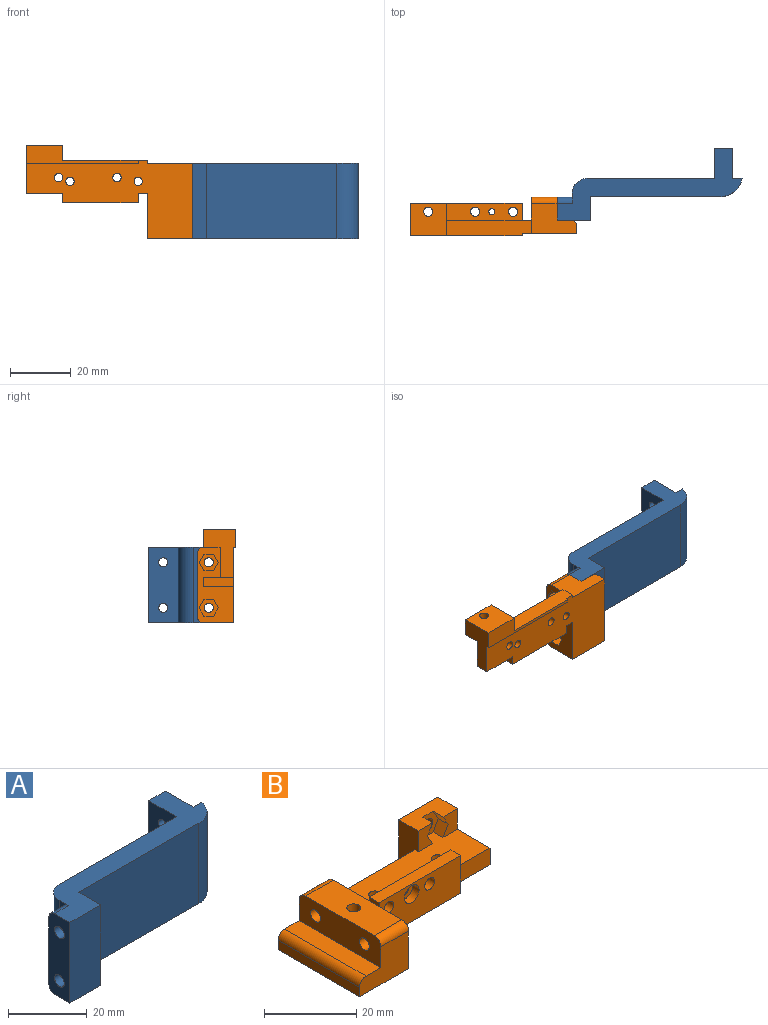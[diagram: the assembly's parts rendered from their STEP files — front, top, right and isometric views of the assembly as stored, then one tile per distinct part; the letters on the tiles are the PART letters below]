
ASSEMBLY  parts=2 mates=1
PART A: 25 faces, bbox 61x23.8x25 mm
  f0: cylinder r=1.75mm len=8mm, axis (1,0,0), area 88mm2, adj f18,f22
  f1: cylinder r=1.75mm len=8mm, axis (1,0,0), area 88mm2, adj f18,f20
  f2: plane 25x10mm, normal (-1,0,0), area 235.9mm2, adj f3,f10,f11,f12,f15,f16
  f3: plane 42x25mm, normal (0,1,0), area 1050mm2, adj f2,f11,f12,f14
  f4: plane 25x3.25mm, normal (-1,0,0), area 33mm2, adj f11,f12,f14,f17,f23,f24
  f5: plane 25x11mm, normal (0,-1,0), area 275mm2, adj f6,f11,f12,f18
  f6: plane 25x7.75mm, normal (1,0,0), area 137.2mm2, adj f5,f7,f11,f12,f19,f21
  f7: plane 43.07x25mm, normal (0,-1,0), area 1076.8mm2, adj f6,f11,f12,f13
  f8: plane 25x3mm, normal (0,1,0), area 75mm2, adj f9,f11,f12,f13
  f9: plane 25x10mm, normal (1,0,0), area 235.9mm2, adj f8,f10,f11,f12,f15,f16
  f10: plane 25x6mm, normal (0,1,0), area 150mm2, adj f2,f9,f11,f12
  f11: plane 61x23.75mm, normal (0,0,1), area 454.6mm2, adj f2,f3,f4,f5,f6,f7,f8,f9
  f12: plane 61x23.75mm, normal (0,0,-1), area 454.6mm2, adj f2,f3,f4,f5,f6,f7,f8,f9
  f13: cylinder r=7mm len=25mm, axis (0,0,1), area 249.8mm2, adj f7,f8,f11,f12
  f14: cylinder r=5mm len=25mm, axis (0,0,1), area 196.3mm2, adj f3,f4,f11,f12
  f15: cylinder r=1.5mm len=6mm, axis (1,0,0), area 56.5mm2, adj f2,f9
  f16: cylinder r=1.5mm len=6mm, axis (1,0,0), area 56.5mm2, adj f2,f9
  f17: plane 21x5mm, normal (0,1,0), area 105mm2, adj f4,f18,f23,f24
  f18: plane 25x7.5mm, normal (-1,0,0), area 166.5mm2, adj f0,f1,f5,f11,f12,f17,f23,f24
  f19: cylinder r=3mm len=6mm, axis (1,0,0), area 56.5mm2, adj f6,f20
  f20: plane 6x6mm, normal (1,0,0), area 18.7mm2, adj f1,f19
  f21: cylinder r=3mm len=6mm, axis (1,0,0), area 56.5mm2, adj f6,f22
  f22: plane 6x6mm, normal (1,0,0), area 18.7mm2, adj f0,f21
  f23: cylinder r=2mm len=5mm, axis (-1,0,0), area 15.7mm2, adj f4,f12,f17,f18
  f24: cylinder r=2mm len=5mm, axis (1,0,0), area 15.7mm2, adj f4,f11,f17,f18
PART B: 63 faces, bbox 55x31x12.8 mm
  f0: plane 5.5x4.41mm, normal (0,-1,0), area 19.9mm2, adj f1,f2,f16,f60,f61
  f1: plane 12x6mm, normal (0,0,1), area 62.5mm2, adj f0,f16,f17,f18,f42,f59,f60,f62
  f2: plane 40x13mm, normal (0,0,1), area 413.8mm2, adj f0,f5,f6,f10,f11,f15,f16,f18
  f3: cylinder r=1mm len=2mm, axis (0,-1,0), area 6.3mm2, adj f20,f34
  f4: plane 25x4.5mm, normal (0,0,1), area 112.5mm2, adj f7,f9,f22,f41
  f5: plane 28x5.25mm, normal (0,1,0), area 144.8mm2, adj f2,f6,f18,f19,f25,f26
  f6: plane 4.5x1mm, normal (-1,0,0), area 4.5mm2, adj f2,f5,f7,f19
  f7: plane 15x10mm, normal (0,1,0), area 113.4mm2, adj f4,f6,f8,f10,f19,f22,f40,f41
  f8: plane 25x2.5mm, normal (-1,0,0), area 62.5mm2, adj f7,f9,f19,f41
  f9: plane 15x10mm, normal (0,-1,0), area 113.4mm2, adj f4,f8,f10,f19,f22,f39,f41
  f10: plane 25x12mm, normal (1,0,0), area 200.9mm2, adj f2,f7,f9,f11,f19,f23,f39,f40
  f11: plane 4.5x3mm, normal (0,-1,0), area 13.5mm2, adj f2,f10,f12,f19
  f12: plane 10x3mm, normal (-1,0,0), area 30mm2, adj f11,f13,f19,f20,f21
  f13: plane 25x10mm, normal (0,-1,0), area 220mm2, adj f12,f14,f19,f21,f31,f32,f33
  f14: plane 10x3mm, normal (1,0,0), area 30mm2, adj f13,f15,f19,f20,f21
  f15: plane 12x4.5mm, normal (0,-1,0), area 54mm2, adj f2,f14,f16,f19
  f16: plane 16x10.75mm, normal (1,0,0), area 109.5mm2, adj f0,f1,f2,f15,f17,f19,f24,f26
  f17: plane 12x10.75mm, normal (0,1,0), area 121.9mm2, adj f1,f16,f18,f26,f43
  f18: plane 10.75x6mm, normal (-1,0,0), area 59.2mm2, adj f1,f2,f5,f17,f26,f42
  f19: plane 55x26mm, normal (0,0,-1), area 829.2mm2, adj f5,f6,f7,f8,f9,f10,f11,f12
  f20: plane 25x5.5mm, normal (0,1,0), area 120.2mm2, adj f2,f3,f12,f14,f21,f31,f32
  f21: plane 25x3mm, normal (0,0,1), area 75mm2, adj f12,f13,f14,f20
  f22: plane 25x7.5mm, normal (-1,0,0), area 171.6mm2, adj f4,f7,f9,f23,f35,f36,f39,f40
  f23: plane 21x8.5mm, normal (0,0,1), area 171.4mm2, adj f10,f22,f37,f39,f40
  f24: plane 37x0.75mm, normal (0,-1,0), area 27.7mm2, adj f16,f19,f25,f26
  f25: plane 1x0.75mm, normal (-1,0,0), area 0.8mm2, adj f5,f19,f24,f26
  f26: plane 37x6mm, normal (0,0,-1), area 97mm2, adj f5,f16,f17,f18,f24,f25
  f27: cylinder r=1.38mm len=4.5mm, axis (0,0,1), area 38.9mm2, adj f2,f19
  f28: cylinder r=1.38mm len=4.5mm, axis (0,0,1), area 38.9mm2, adj f2,f19
  f29: cylinder r=1.38mm len=4.5mm, axis (0,0,1), area 38.9mm2, adj f2,f19
  f30: cylinder r=1.38mm len=4.5mm, axis (0,0,1), area 38.9mm2, adj f2,f19
  f31: cylinder r=1.5mm len=3mm, axis (0,-1,0), area 28.3mm2, adj f13,f20
  f32: cylinder r=1.5mm len=3mm, axis (0,-1,0), area 28.3mm2, adj f13,f20
  f33: cylinder r=2.25mm len=4.5mm, axis (0,-1,0), area 28.3mm2, adj f13,f34
  f34: plane 4.5x4.5mm, normal (0,-1,0), area 12.8mm2, adj f3,f33
  f35: cylinder r=1.5mm len=4mm, axis (-1,0,0), area 37.7mm2, adj f22,f51
  f36: cylinder r=1.5mm len=4mm, axis (-1,0,0), area 37.7mm2, adj f22,f44
  f37: cylinder r=1.5mm len=7.5mm, axis (0,0,1), area 70.7mm2, adj f23,f38
  f38: plane 3x3mm, normal (0,0,1), area 7.1mm2, adj f37
  f39: cylinder r=2mm len=8.5mm, axis (-1,0,0), area 26.7mm2, adj f9,f10,f22,f23
  f40: cylinder r=2mm len=8.5mm, axis (1,0,0), area 26.7mm2, adj f7,f10,f22,f23
  f41: cylinder r=2mm len=25mm, axis (0,1,0), area 78.5mm2, adj f4,f7,f8,f9
  f42: plane 5.5x4.41mm, normal (0,-1,0), area 19.9mm2, adj f1,f2,f18,f58,f59
  f43: cylinder r=1.5mm len=3mm, axis (0,1,0), area 28.3mm2, adj f17,f62
  f44: plane 6.35x5.5mm, normal (1,0,0), area 19.1mm2, adj f36,f45,f46,f47,f48,f49,f50
  f45: plane 4.5x3.18mm, normal (0,1,0), area 14.3mm2, adj f10,f44,f46,f50
  f46: plane 4.5x2.75mm, normal (0,0.5,-0.87), area 14.3mm2, adj f10,f44,f45,f47
  f47: plane 4.5x2.75mm, normal (0,-0.5,-0.87), area 14.3mm2, adj f10,f44,f46,f48
  f48: plane 4.5x3.18mm, normal (0,-1,0), area 14.3mm2, adj f10,f44,f47,f49
  f49: plane 4.5x2.75mm, normal (0,-0.5,0.87), area 14.3mm2, adj f10,f44,f48,f50
  f50: plane 4.5x2.75mm, normal (0,0.5,0.87), area 14.3mm2, adj f10,f44,f45,f49
  f51: plane 6.35x5.5mm, normal (1,0,0), area 19.1mm2, adj f35,f52,f53,f54,f55,f56,f57
  f52: plane 4.5x3.18mm, normal (0,-1,0), area 14.3mm2, adj f10,f51,f53,f57
  f53: plane 4.5x2.75mm, normal (0,-0.5,0.87), area 14.3mm2, adj f10,f51,f52,f54
  f54: plane 4.5x2.75mm, normal (0,0.5,0.87), area 14.3mm2, adj f10,f51,f53,f55
  f55: plane 4.5x3.18mm, normal (0,1,0), area 14.3mm2, adj f10,f51,f54,f56
  f56: plane 4.5x2.75mm, normal (0,0.5,-0.87), area 14.3mm2, adj f10,f51,f55,f57
  f57: plane 4.5x2.75mm, normal (0,-0.5,-0.87), area 14.3mm2, adj f10,f51,f52,f56
  f58: plane 3x2.75mm, normal (0.87,0,0.5), area 9.5mm2, adj f2,f42,f59,f62
  f59: plane 3x2.75mm, normal (0.87,0,-0.5), area 9.5mm2, adj f1,f42,f58,f62
  f60: plane 3x2.75mm, normal (-0.87,0,-0.5), area 9.5mm2, adj f0,f1,f61,f62
  f61: plane 3x2.75mm, normal (-0.87,0,0.5), area 9.5mm2, adj f0,f2,f60,f62
  f62: plane 6.35x5.5mm, normal (0,-1,0), area 19.1mm2, adj f1,f2,f43,f58,f59,f60,f61
PLACE A t=(23.54,-3.88,-7.47)mm
PLACE B rot(axis=(0,0.71,0.71),180deg) t=(-57.96,-19.13,4.53)mm
MATE parallel A.f1 <-> B.f36  axis (-1,0,0) through (-9.46,-10.88,12.53)mm
